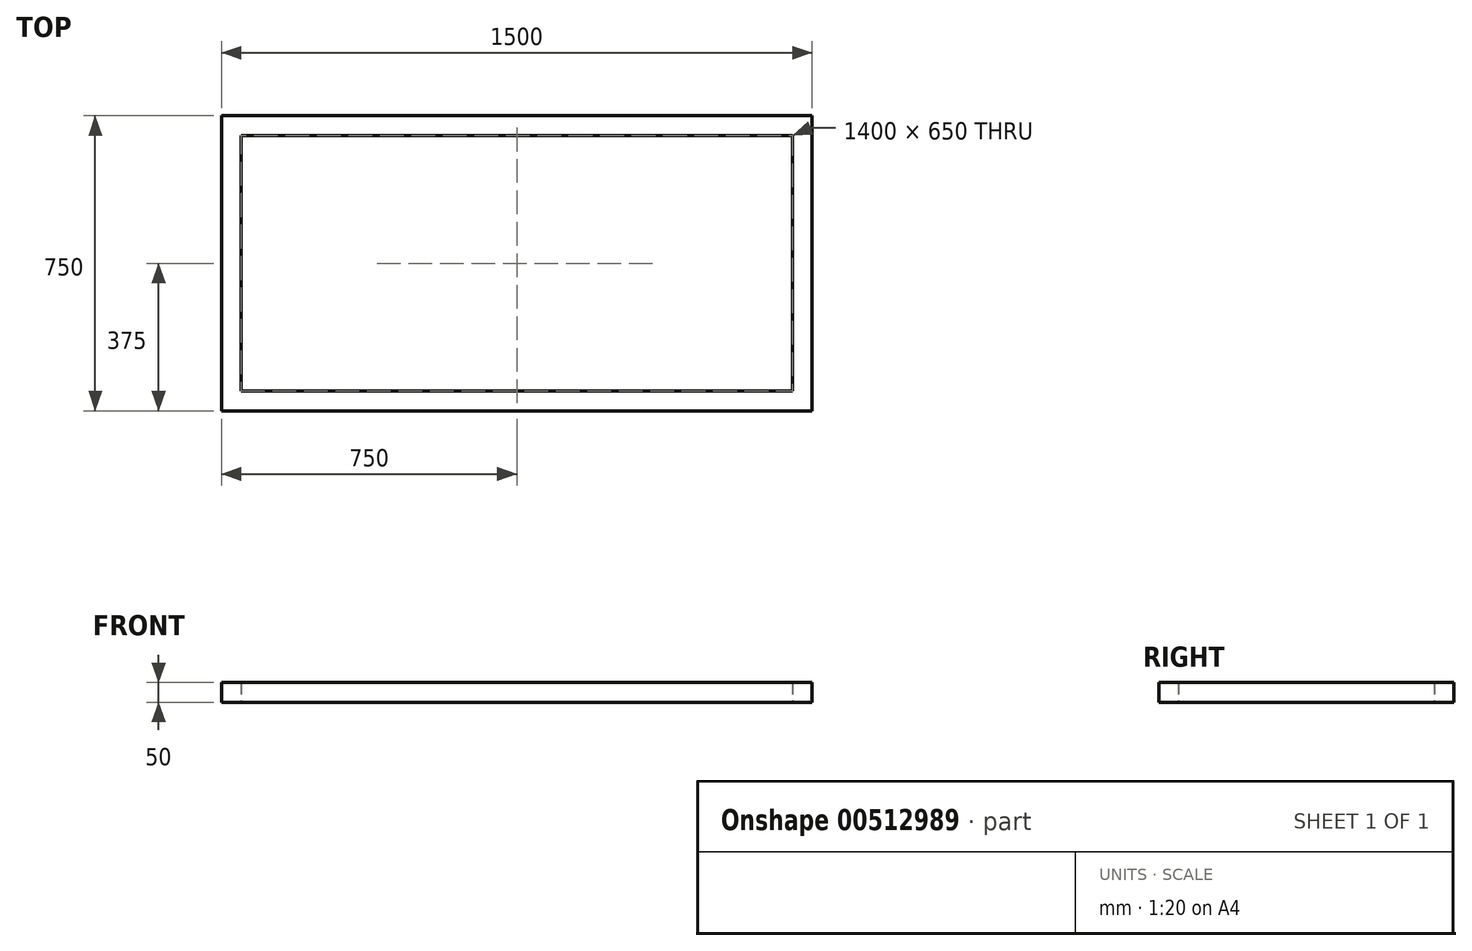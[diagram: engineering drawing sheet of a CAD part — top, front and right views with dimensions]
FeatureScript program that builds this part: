
annotation { "Feature Type Name" : "Feature", "Feature Type Description" : "" }
export const myFeature = defineFeature(function(context is Context, id is Id, definition is map)
    precondition{}
    {
        {
            var Q0;
            Q0=qCreatedBy(makeId("Top.planeOp"),FACE);
            var sketch = newSketch(context, id + "F0", { "sketchPlane" : qUnion([Q0])});
            skLineSegment(sketch, "E0.bottom", {"start": v(-750, -375) * mm, "end": v(750, -375) * mm});
            skLineSegment(sketch, "E0.top", {"start": v(-750, 375) * mm, "end": v(750, 375) * mm});
            skLineSegment(sketch, "E0.left", {"start": v(-750, -375) * mm, "end": v(-750, 375) * mm});
            skLineSegment(sketch, "E0.right", {"start": v(750, -375) * mm, "end": v(750, 375) * mm});
            skPoint(sketch, "E0.middle", {"position": v(0, 0) * mm});
            skLineSegment(sketch, "E1.bottom", {"start": v(-700, -325) * mm, "end": v(700, -325) * mm});
            skLineSegment(sketch, "E1.top", {"start": v(-700, 325) * mm, "end": v(700, 325) * mm});
            skLineSegment(sketch, "E1.left", {"start": v(-700, -325) * mm, "end": v(-700, 325) * mm});
            skLineSegment(sketch, "E1.right", {"start": v(700, -325) * mm, "end": v(700, 325) * mm});
            skLineSegment(sketch, "E2.bottom", {"start": v(-359.72, -375) * mm, "end": v(359.72, -375) * mm});
            skLineSegment(sketch, "E2.top", {"start": v(-359.72, -375) * mm, "end": v(0, -375) * mm});
            skLineSegment(sketch, "E2.left", {"start": v(-359.72, -375) * mm, "end": v(-359.72, -375) * mm});
            skLineSegment(sketch, "E2.right", {"start": v(359.72, -375) * mm, "end": v(359.72, -375) * mm});
            skPoint(sketch, "E2.middle", {"position": v(0, -375) * mm});
            skLineSegment(sketch, "E3.bottom", {"start": v(-359.72, -375) * mm, "end": v(522.34, -375) * mm});
            skPoint(sketch, "E4.middle", {"position": v(0, -2450.12) * mm});
            skPoint(sketch, "E3.top.end.orphan", {"position": v(49, -1629.69) * mm});
            skPoint(sketch, "E4.left.start.orphan", {"position": v(-151, -1629.69) * mm});
            skPoint(sketch, "E4.top.end.orphan", {"position": v(151, -3270.56) * mm});
            skPoint(sketch, "E4.top.start.orphan", {"position": v(-49, -3270.56) * mm});
            skLineSegment(sketch, "E5", {"start": v(0, -375) * mm, "end": v(359.72, -375) * mm});
            skLineSegment(sketch, "E6", {"start": v(-49, -3270.56) * mm, "end": v(151, -3270.56) * mm});
            skLineSegment(sketch, "E7", {"start": v(151, -3270.56) * mm, "end": v(359.72, -375) * mm});
            skLineSegment(sketch, "E8", {"start": v(-49, -3270.56) * mm, "end": v(-359.72, -375) * mm});
            skLineSegment(sketch, "E9", {"start": v(309.72, -375) * mm, "end": v(104.52, -3220.56) * mm});
            skLineSegment(sketch, "E10", {"start": v(104.52, -3220.56) * mm, "end": v(-4.37, -3220.56) * mm});
            skLineSegment(sketch, "E11", {"start": v(-4.37, -3220.56) * mm, "end": v(-309.72, -375) * mm});
            skLineSegment(sketch, "E12", {"start": v(-4.37, -3220.56) * mm, "end": v(-4.37, -3270.56) * mm});
            skLineSegment(sketch, "E13", {"start": v(104.52, -3220.56) * mm, "end": v(104.52, -3270.56) * mm});
            skLineSegment(sketch, "E14", {"start": v(309.72, -375) * mm, "end": v(359.72, -375) * mm});
            skLineSegment(sketch, "E15", {"start": v(-309.72, -375) * mm, "end": v(-359.72, -375) * mm});
            skLineSegment(sketch, "E16", {"start": v(154.5, -3221.91) * mm, "end": v(104.52, -3220.56) * mm});
            skSolve(sketch);
        }
        {
            var Q0;
            Q0=makeQuery(id+"F0.imprint","IMPRINT",FACE,{"disambiguationData":[TD([[makeQuery(id+"F0.imprint","IMPRINT",EDGE,{"derivedFrom":sQuery(id+"F0.wireOp",EDGE,"E0.top")}),-1.0]])]});
            extrude(context, id + "F1", {"entities" : qUnion([Q0]), "endBound" : BoundingType.SYMMETRIC, "depth" : 50 * mm});
        }
    });
